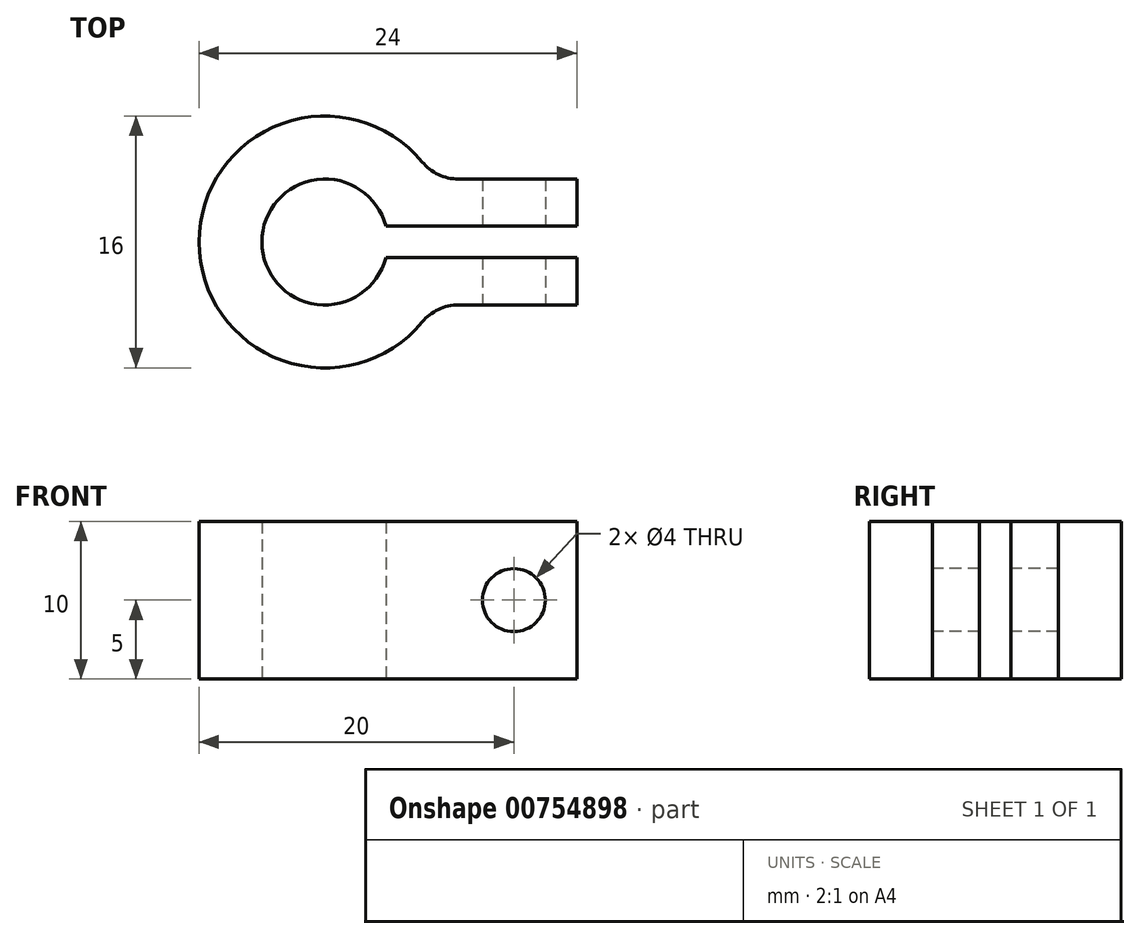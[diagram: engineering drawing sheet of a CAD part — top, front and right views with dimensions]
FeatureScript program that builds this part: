
annotation { "Feature Type Name" : "Feature", "Feature Type Description" : "" }
export const myFeature = defineFeature(function(context is Context, id is Id, definition is map)
    precondition{}
    {
        {
            var Q0;
            Q0=qCreatedBy(makeId("Top.planeOp"),FACE);
            var sketch = newSketch(context, id + "F0", { "sketchPlane" : qUnion([Q0])});
            skArc(sketch, "E0", {"start": v(3.87, 1) * mm, "mid": v(-4, 0) * mm, "end": v(3.87, -1) * mm});
            skArc(sketch, "E1", {"start": v(6.17, 5.1) * mm, "mid": v(-8, 0) * mm, "end": v(6.17, -5.1) * mm});
            skLineSegment(sketch, "E2.bottom", {"start": v(8.49, 4) * mm, "end": v(16, 4) * mm});
            skLineSegment(sketch, "E2.top", {"start": v(3.87, 1) * mm, "end": v(16, 1) * mm});
            skLineSegment(sketch, "E2.right", {"start": v(16, 4) * mm, "end": v(16, 1) * mm});
            skLineSegment(sketch, "E3", {"start": v(0, 0) * mm, "end": v(20.62, 0) * mm, "construction": true});
            skLineSegment(sketch, "E4.MirrorCS", {"start": v(3.87, -1) * mm, "end": v(16, -1) * mm});
            skLineSegment(sketch, "E5.MirrorCS", {"start": v(16, -4) * mm, "end": v(16, -1) * mm});
            skLineSegment(sketch, "E6.MirrorCS", {"start": v(8.49, -4) * mm, "end": v(16, -4) * mm});
            skPoint(sketch, "E2.left.end.orphan", {"position": v(4, 1) * mm});
            skPoint(sketch, "E2.left.start.orphan", {"position": v(0, 4) * mm});
            skPoint(sketch, "E7.orphan", {"position": v(4, -1) * mm});
            skPoint(sketch, "E8.orphan", {"position": v(0, -4) * mm});
            skPoint(sketch, "E9.visualSharp", {"position": v(6.93, 4) * mm});
            skArc(sketch, "E9.filletArc", {"start": v(6.17, 5.1) * mm, "mid": v(7.2, 4.29) * mm, "end": v(8.49, 4) * mm});
            skPoint(sketch, "E10.visualSharp", {"position": v(6.93, -4) * mm});
            skArc(sketch, "E10.filletArc", {"start": v(8.49, -4) * mm, "mid": v(7.2, -4.29) * mm, "end": v(6.17, -5.1) * mm});
            skSolve(sketch);
        }
        {
            var Q0;
            Q0 = qSketchRegion(id + "F0", true);
            extrude(context, id + "F1", {"entities" : qUnion([Q0]), "depth" : 10 * mm, "offsetDistance" : 25 * mm});
        }
        {
            var Q0;
            Q0=makeQuery(id+"F1.opExtrude","SWEPT_FACE",FACE,{"disambiguationData":[OSD([sQuery(id+"F0.wireOp",EDGE,"E6.MirrorCS")])]});
            var sketch = newSketch(context, id + "F2", { "sketchPlane" : qUnion([Q0])});
            skCircle(sketch, "E11", {"center": v(12, 5) * mm, "radius": 2 * mm});
            skSolve(sketch);
        }
        {
            var Q0;
            Q0=makeQuery(id+"F2.imprint","IMPRINT",FACE,{"disambiguationData":[TD([[makeQuery(id+"F2.imprint","IMPRINT",EDGE,{"derivedFrom":sQuery(id+"F2.wireOp",EDGE,"E11")}),1.0]])]});
            extrude(context, id + "F3", {"entities" : qUnion([Q0]), "operationType" : NewBodyOperationType.REMOVE, "endBound" : BoundingType.THROUGH_ALL, "oppositeDirection" : true, "depth" : 25 * mm, "offsetDistance" : 25 * mm});
        }
    });
